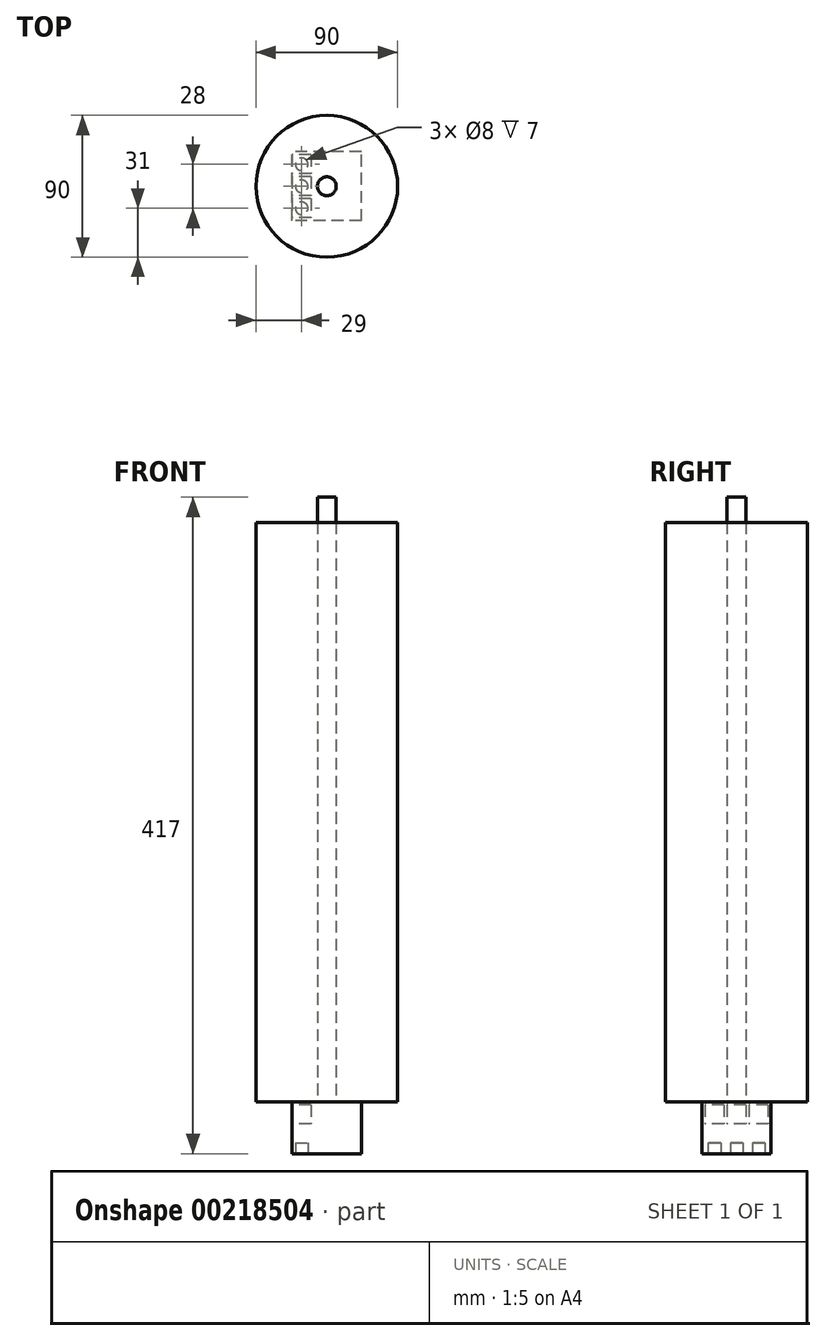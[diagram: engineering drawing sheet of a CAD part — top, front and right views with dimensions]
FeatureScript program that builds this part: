
annotation { "Feature Type Name" : "Feature", "Feature Type Description" : "" }
export const myFeature = defineFeature(function(context is Context, id is Id, definition is map)
    precondition{}
    {
        {
            var Q0;
            Q0=qCreatedBy(makeId("Top.planeOp"),FACE);
            var sketch = newSketch(context, id + "F0", { "sketchPlane" : qUnion([Q0])});
            skCircle(sketch, "E0", {"center": v(0, 0) * mm, "radius": 45 * mm});
            skCircle(sketch, "E1", {"center": v(0, 0) * mm, "radius": 6 * mm});
            skLineSegment(sketch, "E2.bottom", {"start": v(22, -22) * mm, "end": v(-22, -22) * mm});
            skLineSegment(sketch, "E2.top", {"start": v(22, 22) * mm, "end": v(-22, 22) * mm});
            skLineSegment(sketch, "E2.left", {"start": v(22, -22) * mm, "end": v(22, 22) * mm});
            skLineSegment(sketch, "E2.right", {"start": v(-22, -22) * mm, "end": v(-22, 22) * mm});
            skSolve(sketch);
        }
        {
            var Q0;
            Q0 = qSketchRegion(id + "F0", true);
            var Q1;
            Q1=makeQuery(id+"F0.imprint","IMPRINT",FACE,{"disambiguationData":[TD([[makeQuery(id+"F0.imprint","IMPRINT",EDGE,{"derivedFrom":sQuery(id+"F0.wireOp",EDGE,"E1")}),-1.0]])]});
            var Q2;
            Q2=makeQuery(id+"F0.imprint","IMPRINT",FACE,{"disambiguationData":[TD([[makeQuery(id+"F0.imprint","IMPRINT",EDGE,{"derivedFrom":sQuery(id+"F0.wireOp",EDGE,"E1")}),1.0]])]});
            extrude(context, id + "F1", {"entities" : qUnion([Q0, Q1, Q2]), "depth" : 368 * mm});
        }
        {
            var Q0;
            Q0=makeQuery(id+"F0.imprint","IMPRINT",FACE,{"disambiguationData":[TD([[makeQuery(id+"F0.imprint","IMPRINT",EDGE,{"derivedFrom":sQuery(id+"F0.wireOp",EDGE,"E1")}),-1.0]])]});
            var Q1;
            Q1=makeQuery(id+"F0.imprint","IMPRINT",FACE,{"disambiguationData":[TD([[makeQuery(id+"F0.imprint","IMPRINT",EDGE,{"derivedFrom":sQuery(id+"F0.wireOp",EDGE,"E1")}),1.0]])]});
            extrude(context, id + "F2", {"entities" : qUnion([Q0, Q1]), "operationType" : NewBodyOperationType.ADD, "oppositeDirection" : true, "depth" : 33 * mm});
        }
        {
            var Q0;
            Q0=makeQuery(id+"F0.imprint","IMPRINT",FACE,{"disambiguationData":[TD([[makeQuery(id+"F0.imprint","IMPRINT",EDGE,{"derivedFrom":sQuery(id+"F0.wireOp",EDGE,"E1")}),1.0]])]});
            extrude(context, id + "F3", {"entities" : qUnion([Q0]), "depth" : 384 * mm});
        }
        {
            var Q0;
            Q0=makeQuery(id+"F2.opExtrude","SWEPT_FACE",FACE,{"disambiguationData":[OSD([sQuery(id+"F0.wireOp",EDGE,"E2.right")])]});
            var sketch = newSketch(context, id + "F4", { "sketchPlane" : qUnion([Q0])});
            skLineSegment(sketch, "E3.bottom", {"start": v(8, -2) * mm, "end": v(20, -2) * mm});
            skLineSegment(sketch, "E3.top", {"start": v(8, -14) * mm, "end": v(20, -14) * mm});
            skLineSegment(sketch, "E3.left", {"start": v(8, -2) * mm, "end": v(8, -14) * mm});
            skLineSegment(sketch, "E3.right", {"start": v(20, -2) * mm, "end": v(20, -14) * mm});
            skPoint(sketch, "E3.middle", {"position": v(14, -8) * mm});
            skLineSegment(sketch, "E4.bottom", {"start": v(-20, -2) * mm, "end": v(-8, -2) * mm});
            skLineSegment(sketch, "E4.top", {"start": v(-20, -14) * mm, "end": v(-8, -14) * mm});
            skLineSegment(sketch, "E4.left", {"start": v(-20, -2) * mm, "end": v(-20, -14) * mm});
            skLineSegment(sketch, "E4.right", {"start": v(-8, -2) * mm, "end": v(-8, -14) * mm});
            skPoint(sketch, "E4.middle", {"position": v(-14, -8) * mm});
            skLineSegment(sketch, "E5.bottom", {"start": v(-6, -2) * mm, "end": v(6, -2) * mm});
            skLineSegment(sketch, "E5.top", {"start": v(-6, -14) * mm, "end": v(6, -14) * mm});
            skLineSegment(sketch, "E5.left", {"start": v(-6, -2) * mm, "end": v(-6, -14) * mm});
            skLineSegment(sketch, "E5.right", {"start": v(6, -2) * mm, "end": v(6, -14) * mm});
            skPoint(sketch, "E5.middle", {"position": v(0, -8) * mm});
            skSolve(sketch);
        }
        {
            var Q0;
            Q0=makeQuery(id+"F4.imprint","IMPRINT",FACE,{"disambiguationData":[TD([[makeQuery(id+"F4.imprint","IMPRINT",EDGE,{"derivedFrom":sQuery(id+"F4.wireOp",EDGE,"E3.bottom")}),-1.0]])]});
            var Q1;
            Q1=makeQuery(id+"F4.imprint","IMPRINT",FACE,{"disambiguationData":[TD([[makeQuery(id+"F4.imprint","IMPRINT",EDGE,{"derivedFrom":sQuery(id+"F4.wireOp",EDGE,"E5.bottom")}),-1.0]])]});
            var Q2;
            Q2=makeQuery(id+"F4.imprint","IMPRINT",FACE,{"disambiguationData":[TD([[makeQuery(id+"F4.imprint","IMPRINT",EDGE,{"derivedFrom":sQuery(id+"F4.wireOp",EDGE,"E4.bottom")}),-1.0]])]});
            extrude(context, id + "F5", {"entities" : qUnion([Q0, Q1, Q2]), "operationType" : NewBodyOperationType.REMOVE, "oppositeDirection" : true, "depth" : 12 * mm});
        }
        {
            var Q0;
            Q0=makeQuery(id+"F2.opExtrude","CAP_FACE",FACE,{"disambiguationData":[OSD([sQuery(id+"F0.wireOp",EDGE,"E2.bottom"),sQuery(id+"F0.wireOp",EDGE,"E2.top"),sQuery(id+"F0.wireOp",EDGE,"E2.left"),sQuery(id+"F0.wireOp",EDGE,"E2.right")])],"isStart":false});
            var sketch = newSketch(context, id + "F6", { "sketchPlane" : qUnion([Q0])});
            skCircle(sketch, "E6", {"center": v(-16, 14) * mm, "radius": 4 * mm});
            skCircle(sketch, "E7", {"center": v(-16, -14) * mm, "radius": 4 * mm});
            skCircle(sketch, "E8", {"center": v(-16, 0) * mm, "radius": 4 * mm});
            skSolve(sketch);
        }
        {
            var Q0;
            Q0=makeQuery(id+"F6.imprint","IMPRINT",FACE,{"disambiguationData":[TD([[makeQuery(id+"F6.imprint","IMPRINT",EDGE,{"derivedFrom":sQuery(id+"F6.wireOp",EDGE,"E6")}),1.0]])]});
            var Q1;
            Q1=makeQuery(id+"F6.imprint","IMPRINT",FACE,{"disambiguationData":[TD([[makeQuery(id+"F6.imprint","IMPRINT",EDGE,{"derivedFrom":sQuery(id+"F6.wireOp",EDGE,"E8")}),1.0]])]});
            var Q2;
            Q2=makeQuery(id+"F6.imprint","IMPRINT",FACE,{"disambiguationData":[TD([[makeQuery(id+"F6.imprint","IMPRINT",EDGE,{"derivedFrom":sQuery(id+"F6.wireOp",EDGE,"E7")}),1.0]])]});
            extrude(context, id + "F7", {"entities" : qUnion([Q0, Q1, Q2]), "operationType" : NewBodyOperationType.REMOVE, "oppositeDirection" : true, "depth" : 7 * mm});
        }
    });
